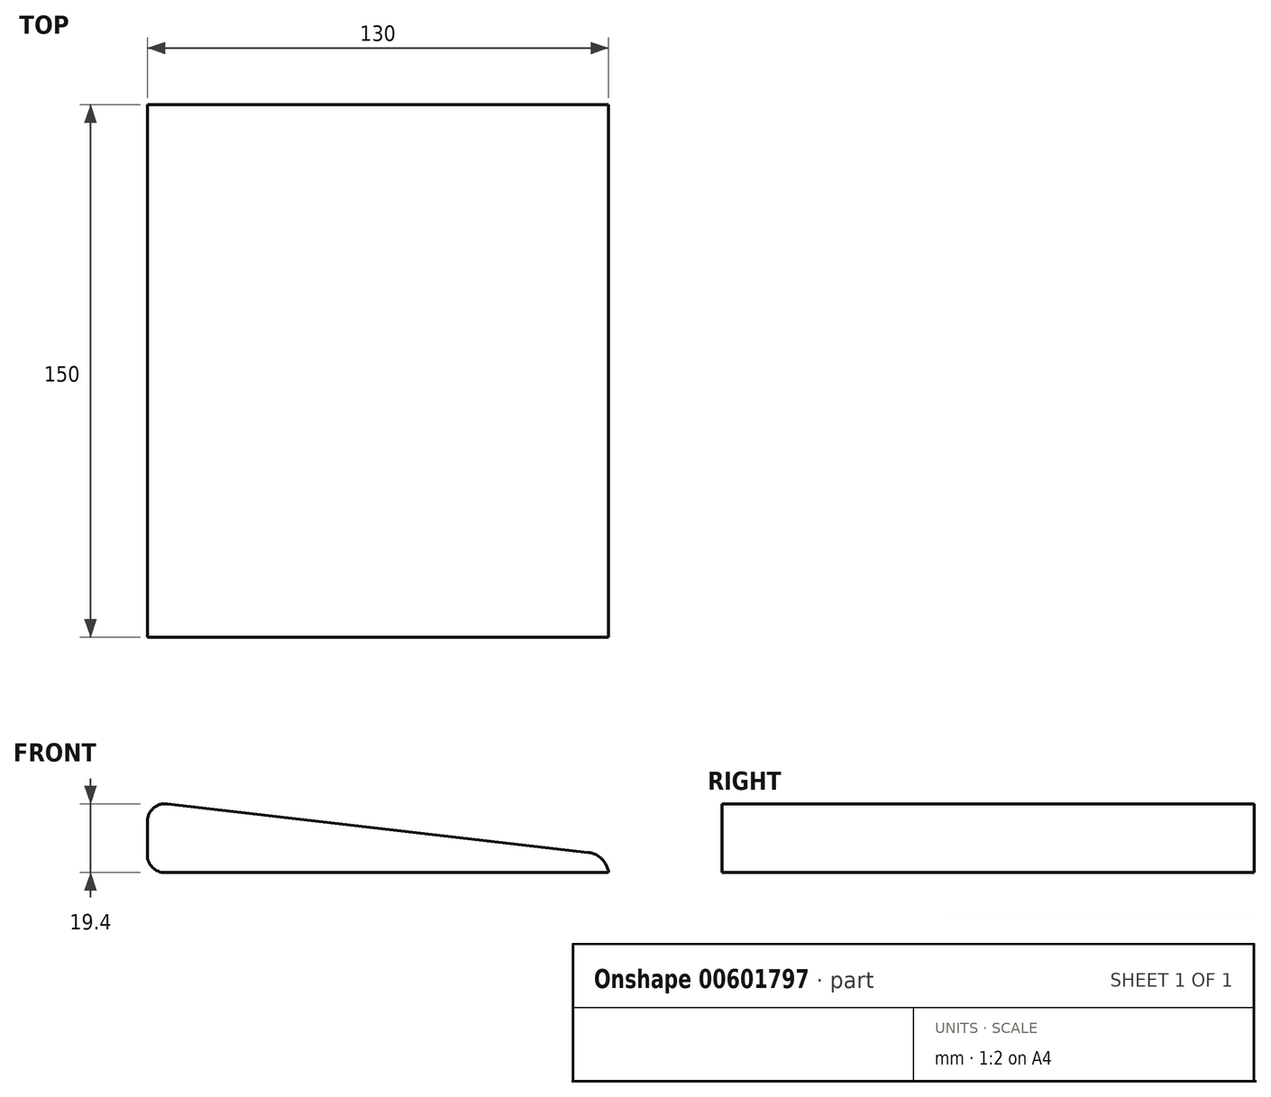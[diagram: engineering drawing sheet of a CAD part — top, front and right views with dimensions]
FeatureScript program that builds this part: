
annotation { "Feature Type Name" : "Feature", "Feature Type Description" : "" }
export const myFeature = defineFeature(function(context is Context, id is Id, definition is map)
    precondition{}
    {
        {
            var Q0;
            Q0=qCreatedBy(makeId("Front.planeOp"),FACE);
            var sketch = newSketch(context, id + "F0", { "sketchPlane" : qUnion([Q0])});
            skLineSegment(sketch, "E0", {"start": v(-82.32, -7.79) * mm, "end": v(-82.32, 12.21) * mm});
            skLineSegment(sketch, "E1", {"start": v(-82.32, -7.79) * mm, "end": v(47.68, -7.79) * mm});
            skLineSegment(sketch, "E2", {"start": v(-82.32, 12.21) * mm, "end": v(41.91, -2.1) * mm});
            skArc(sketch, "E3", {"start": v(47.68, -7.79) * mm, "mid": v(45.78, -3.95) * mm, "end": v(41.91, -2.1) * mm});
            skSolve(sketch);
        }
        {
            var Q0;
            Q0=makeQuery(id+"F0.imprint","IMPRINT",FACE,{"disambiguationData":[TD([[makeQuery(id+"F0.imprint","IMPRINT",EDGE,{"derivedFrom":sQuery(id+"F0.wireOp",EDGE,"E0")}),-1.0]])]});
            extrude(context, id + "F1", {"entities" : qUnion([Q0]), "depth" : 150 * mm, "offsetDistance" : 25 * mm});
        }
        {
            var Q0;
            Q0=makeQuery(id+"F1.opExtrude","SWEPT_EDGE",EDGE,{"disambiguationData":[OSD([sQuery(id+"F0.wireOp",EDGE,"E0"),sQuery(id+"F0.wireOp",EDGE,"VKQ5jxaC-0wzA-Lfjx-VAjg-Lw4MtnmORvU9")])]});
            fillet(context, id + "F2", {"entities" : qUnion([Q0]), "radius" : 5 * mm, "tangentPropagation" : true, "allowEdgeOverflow" : false});
        }
    });
